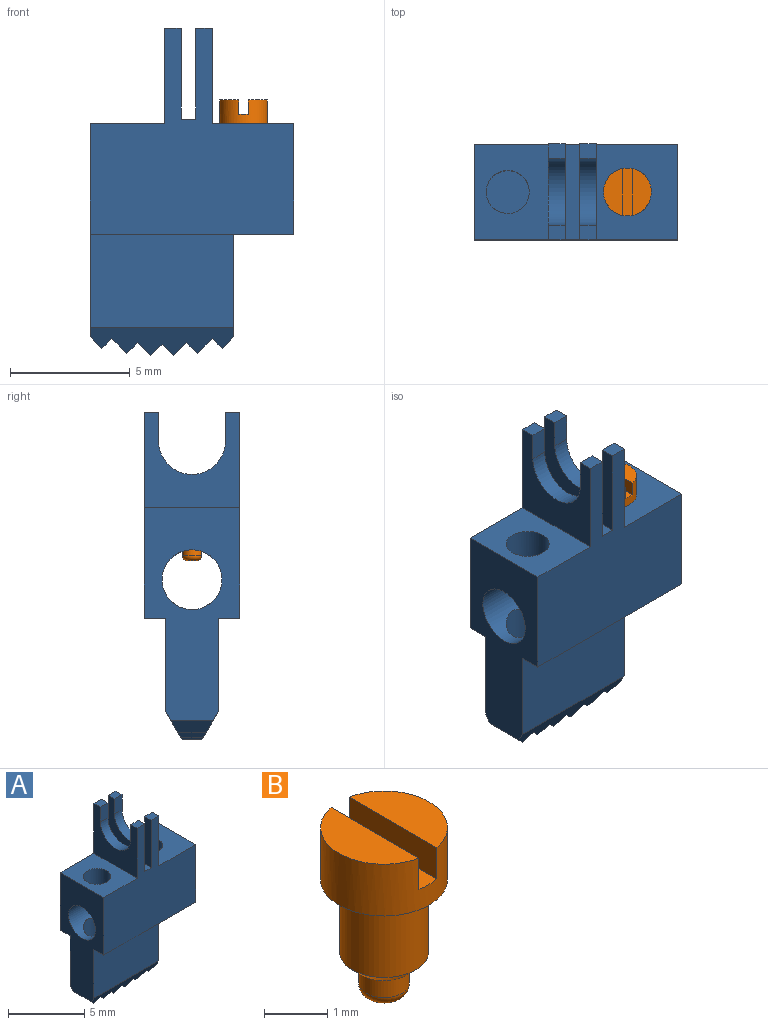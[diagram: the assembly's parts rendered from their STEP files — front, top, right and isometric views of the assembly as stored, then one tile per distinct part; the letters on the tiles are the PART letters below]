
ASSEMBLY  parts=2 mates=1
PART A: 44 faces, bbox 8.5x4x13.7 mm
  f0: plane 4.3x2.2mm, normal (1,0,0), area 9.4mm2, adj f1,f2,f10,f19,f20,f32
  f1: plane 6x1.19mm, normal (0,0.87,-0.5), area 5.6mm2, adj f0,f16,f20,f32,f33,f34,f35,f36
  f2: plane 6x1.19mm, normal (0,-0.87,-0.5), area 5.6mm2, adj f0,f16,f19,f32,f33,f34,f35,f36
  f3: plane 0.7x0.6mm, normal (0,0,1), area 0.4mm2, adj f5,f13,f18,f24
  f4: plane 0.7x0.6mm, normal (0,0,1), area 0.4mm2, adj f5,f13,f17,f25
  f5: plane 4x3.8mm, normal (-1,0,0), area 8.8mm2, adj f3,f4,f14,f17,f18,f24,f25,f26
  f6: plane 4x3.8mm, normal (1,0,0), area 8.8mm2, adj f7,f8,f14,f17,f18,f21,f22,f23
  f7: plane 0.7x0.6mm, normal (0,0,1), area 0.4mm2, adj f6,f9,f18,f23
  f8: plane 0.7x0.6mm, normal (0,0,1), area 0.4mm2, adj f6,f9,f17,f22
  f9: plane 4x4mm, normal (-1,0,0), area 9.6mm2, adj f7,f8,f15,f17,f18,f21,f22,f23
  f10: plane 8.5x4mm, normal (0,0,-1), area 20.8mm2, adj f0,f11,f16,f17,f18,f19,f20
  f11: plane 4.6x4mm, normal (1,0,0), area 13.5mm2, adj f10,f12,f17,f18,f27
  f12: plane 4x3.4mm, normal (0,0,1), area 11.8mm2, adj f11,f13,f17,f18,f28
  f13: plane 4x4mm, normal (1,0,0), area 9.6mm2, adj f3,f4,f12,f17,f18,f24,f25,f26
  f14: plane 4x0.6mm, normal (0,0,1), area 2.4mm2, adj f5,f6,f17,f18
  f15: plane 4x3.1mm, normal (0,0,1), area 9.9mm2, adj f9,f16,f17,f18,f29
  f16: plane 8.9x4mm, normal (-1,0,0), area 22.9mm2, adj f1,f2,f10,f15,f17,f18,f19,f20
  f17: plane 8.6x8.5mm, normal (0,-1,0), area 44.8mm2, adj f4,f5,f6,f8,f9,f10,f11,f12
  f18: plane 8.6x8.5mm, normal (0,1,0), area 44.8mm2, adj f3,f5,f6,f7,f9,f10,f11,f12
  f19: plane 6x3.9mm, normal (0,-1,0), area 23.4mm2, adj f0,f2,f10,f16
  f20: plane 6x3.9mm, normal (0,1,0), area 23.4mm2, adj f0,f1,f10,f16
  f21: cylinder r=1.4mm len=2.8mm, axis (1,0,0), area 3.1mm2, adj f6,f9,f22,f23
  f22: plane 1.2x0.7mm, normal (0,1,0), area 0.8mm2, adj f6,f8,f9,f21
  f23: plane 1.2x0.7mm, normal (0,-1,0), area 0.8mm2, adj f6,f7,f9,f21
  f24: plane 1.2x0.7mm, normal (0,-1,0), area 0.8mm2, adj f3,f5,f13,f26
  f25: plane 1.2x0.7mm, normal (0,1,0), area 0.8mm2, adj f4,f5,f13,f26
  f26: cylinder r=1.4mm len=2.8mm, axis (1,0,0), area 3.1mm2, adj f5,f13,f24,f25
  f27: cylinder r=1.25mm len=8.5mm, axis (1,0,0), area 59.4mm2, adj f11,f16,f28,f29,f30
  f28: cylinder r=0.75mm len=2mm, axis (0,0,1), area 8.8mm2, adj f12,f27
  f29: cylinder r=0.9mm len=2.13mm, axis (0,0,1), area 10.9mm2, adj f15,f27
  f30: cylinder r=0.9mm len=3.83mm, axis (0,0,1), area 20.5mm2, adj f27,f31
  f31: plane 1.8x1.8mm, normal (0,0,1), area 2.5mm2, adj f30
  f32: plane 1.74x0.48mm, normal (0.71,0,-0.71), area 1mm2, adj f0,f1,f2,f33
  f33: plane 1.66x0.41mm, normal (-0.71,0,-0.71), area 0.8mm2, adj f1,f2,f32,f34
  f34: plane 1.66x0.63mm, normal (0.71,0,-0.71), area 1.2mm2, adj f1,f2,f33,f35
  f35: plane 1.46x0.45mm, normal (-0.71,0,-0.71), area 0.8mm2, adj f1,f2,f34,f36
  f36: plane 1.46x0.54mm, normal (0.71,0,-0.71), area 0.9mm2, adj f1,f2,f35,f37
  f37: plane 1.39x0.49mm, normal (-0.71,0,-0.71), area 0.8mm2, adj f1,f2,f36,f38
  f38: plane 1.39x0.49mm, normal (0.71,0,-0.71), area 0.8mm2, adj f1,f2,f37,f39
  f39: plane 1.46x0.54mm, normal (-0.71,0,-0.71), area 0.9mm2, adj f1,f2,f38,f40
  f40: plane 1.46x0.45mm, normal (0.71,0,-0.71), area 0.8mm2, adj f1,f2,f39,f41
  f41: plane 1.66x0.63mm, normal (-0.71,0,-0.71), area 1.2mm2, adj f1,f2,f40,f42
  f42: plane 1.66x0.41mm, normal (0.71,0,-0.71), area 0.8mm2, adj f1,f2,f41,f43
  f43: plane 1.74x0.48mm, normal (-0.71,0,-0.71), area 1mm2, adj f1,f2,f16,f42
PART B: 13 faces, bbox 2x2x3.2 mm
  f0: plane 1.96x0.8mm, normal (0,0,1), area 1.2mm2, adj f2,f10
  f1: plane 1.96x0.8mm, normal (0,0,1), area 1.2mm2, adj f2,f11
  f2: cylinder r=1mm len=2mm, axis (0,0,1), area 5.8mm2, adj f0,f1,f9,f10,f11,f12
  f3: plane 0.4x0.4mm, normal (0,0,-1), area 0.1mm2, adj f4
  f4: torus R=0.2mm, axis (0,0,1), area 0.6mm2, adj f3,f5
  f5: cylinder r=0.4mm len=0.8mm, axis (0,0,1), area 1mm2, adj f4,f6
  f6: plane 1x1mm, normal (0,0,-1), area 0.3mm2, adj f5,f7
  f7: cone r=0.5mm half-angle=45deg, axis (0,0,1), area 1.1mm2, adj f6,f8
  f8: cylinder r=0.7mm len=1.4mm, axis (0,0,1), area 6.2mm2, adj f7,f9
  f9: plane 2x2mm, normal (0,0,-1), area 1.6mm2, adj f2,f8
  f10: plane 1.96x0.6mm, normal (-1,0,0), area 1.2mm2, adj f0,f2,f12
  f11: plane 1.96x0.6mm, normal (1,0,0), area 1.2mm2, adj f1,f2,f12
  f12: plane 2x0.4mm, normal (0,0,1), area 0.8mm2, adj f2,f10,f11
PLACE A t=(0,-2.5,0)mm
PLACE B t=(0.4,-2.5,7.5)mm
MATE fastened B.f2 <-> A.f28  axis (0,0,1) through (0.4,-2.5,9.7)mm
